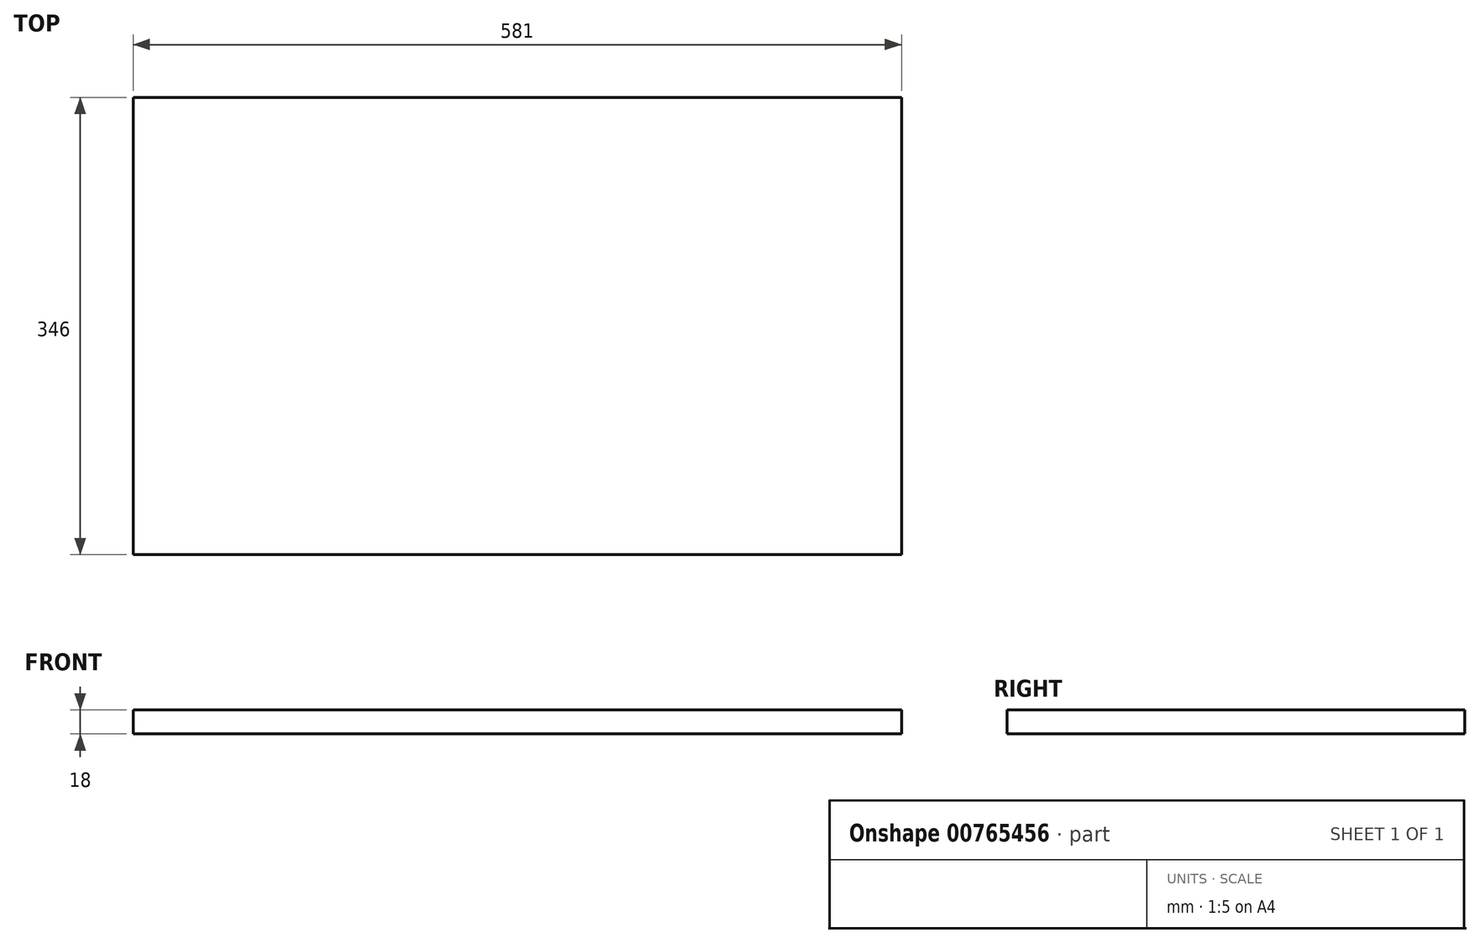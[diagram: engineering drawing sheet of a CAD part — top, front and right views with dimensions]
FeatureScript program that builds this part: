
annotation { "Feature Type Name" : "Feature", "Feature Type Description" : "" }
export const myFeature = defineFeature(function(context is Context, id is Id, definition is map)
    precondition{}
    {
        {
            var Q0;
            Q0=qCreatedBy(makeId("Top.planeOp"),FACE);
            var sketch = newSketch(context, id + "F0", { "sketchPlane" : qUnion([Q0])});
            skLineSegment(sketch, "E0.bottom", {"start": v(-290.5, -173) * mm, "end": v(290.5, -173) * mm});
            skLineSegment(sketch, "E0.top", {"start": v(-290.5, 173) * mm, "end": v(290.5, 173) * mm});
            skLineSegment(sketch, "E0.left", {"start": v(-290.5, -173) * mm, "end": v(-290.5, 173) * mm});
            skLineSegment(sketch, "E0.right", {"start": v(290.5, -173) * mm, "end": v(290.5, 173) * mm});
            skPoint(sketch, "E0.middle", {"position": v(0, 0) * mm});
            skSolve(sketch);
        }
        {
            var Q0;
            Q0 = qSketchRegion(id + "F0", true);
            extrude(context, id + "F1", {"entities" : qUnion([Q0]), "depth" : 18 * mm, "offsetDistance" : 25 * mm});
        }
    });
